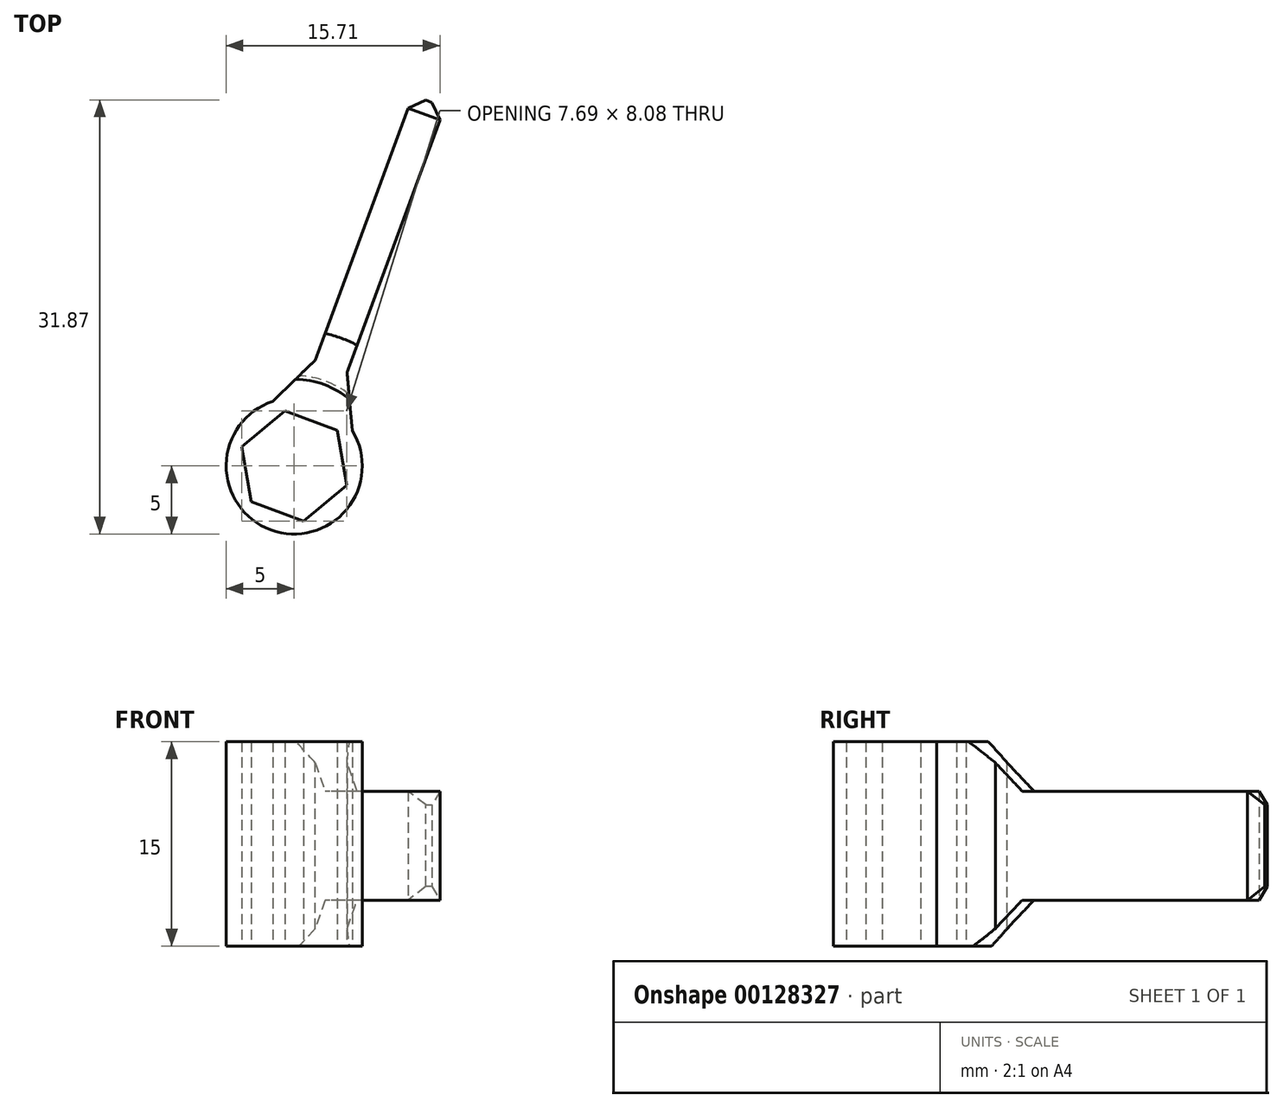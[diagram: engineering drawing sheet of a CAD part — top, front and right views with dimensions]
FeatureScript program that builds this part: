
annotation { "Feature Type Name" : "Feature", "Feature Type Description" : "" }
export const myFeature = defineFeature(function(context is Context, id is Id, definition is map)
    precondition{}
    {
        {
            var Q0;
            Q0=qCreatedBy(makeId("Top.planeOp"),FACE);
            var sketch = newSketch(context, id + "F0", { "sketchPlane" : qUnion([Q0])});
            skCircle(sketch, "E0", {"center": v(0, 0) * mm, "radius": 5 * mm});
            skCircle(sketch, "E1.cCircle", {"center": v(0, 0) * mm, "radius": 4.1 * mm, "construction": true});
            skLineSegment(sketch, "E1.0", {"start": v(3.85, -1.42) * mm, "end": v(0.7, -4.04) * mm});
            skLineSegment(sketch, "E1.1", {"start": v(0.7, -4.04) * mm, "end": v(-3.15, -2.62) * mm});
            skLineSegment(sketch, "E1.2", {"start": v(-3.15, -2.62) * mm, "end": v(-3.85, 1.42) * mm});
            skLineSegment(sketch, "E1.3", {"start": v(-3.85, 1.42) * mm, "end": v(-0.7, 4.04) * mm});
            skLineSegment(sketch, "E1.4", {"start": v(-0.7, 4.04) * mm, "end": v(3.15, 2.62) * mm});
            skLineSegment(sketch, "E1.5", {"start": v(3.15, 2.62) * mm, "end": v(3.85, -1.42) * mm});
            skSolve(sketch);
        }
        {
            var Q0;
            Q0 = qSketchRegion(id + "F0", true);
            extrude(context, id + "F1", {"entities" : qUnion([Q0]), "depth" : 15 * mm});
        }
        {
            var Q0;
            Q0=makeQuery(id+"F1.opExtrude","SWEPT_FACE",FACE,{"disambiguationData":[OSD([sQuery(id+"F0.wireOp",EDGE,"E1.4")])]});
            var sketch = newSketch(context, id + "F2", { "sketchPlane" : qUnion([Q0])});
            skLineSegment(sketch, "E2.bottom", {"start": v(1.25, 11.37) * mm, "end": v(-1.25, 11.37) * mm});
            skLineSegment(sketch, "E2.top", {"start": v(1.25, 3.37) * mm, "end": v(-1.25, 3.37) * mm});
            skLineSegment(sketch, "E2.left", {"start": v(1.25, 11.37) * mm, "end": v(1.25, 3.37) * mm});
            skLineSegment(sketch, "E2.right", {"start": v(-1.25, 11.37) * mm, "end": v(-1.25, 3.37) * mm});
            skPoint(sketch, "E3", {"position": v(0, 11.37) * mm});
            skPoint(sketch, "E4", {"position": v(0, 15) * mm});
            skSolve(sketch);
        }
        {
            var Q0;
            Q0=makeQuery(id+"F2.imprint","IMPRINT",FACE,{"disambiguationData":[TD([[makeQuery(id+"F2.imprint","IMPRINT",EDGE,{"derivedFrom":sQuery(id+"F2.wireOp",EDGE,"E2.bottom")}),1.0]])]});
            extrude(context, id + "F3", {"entities" : qUnion([Q0]), "operationType" : NewBodyOperationType.ADD, "oppositeDirection" : true, "depth" : 25 * mm});
        }
        {
            var Q0;
            Q0=makeQuery(id+"F3.boolean.opBoolean","INTERSECT",EDGE,{"derivedFrom":[makeQuery(id+"F1.opExtrude","SWEPT_FACE",FACE,{"disambiguationData":[OSD([sQuery(id+"F0.wireOp",EDGE,"E0")])]}),makeQuery(id+"F3.opExtrude","SWEPT_FACE",FACE,{"disambiguationData":[OSD([sQuery(id+"F2.wireOp",EDGE,"E2.bottom")])]})]});
            var Q1;
            Q1=makeQuery(id+"F3.boolean.opBoolean","INTERSECT",EDGE,{"derivedFrom":[makeQuery(id+"F1.opExtrude","SWEPT_FACE",FACE,{"disambiguationData":[OSD([sQuery(id+"F0.wireOp",EDGE,"E0")])]}),makeQuery(id+"F3.opExtrude","SWEPT_FACE",FACE,{"disambiguationData":[OSD([sQuery(id+"F2.wireOp",EDGE,"E2.top")])]})]});
            var Q2;
            Q2=makeQuery(id+"F3.boolean.opBoolean","INTERSECT",EDGE,{"derivedFrom":[makeQuery(id+"F1.opExtrude","SWEPT_FACE",FACE,{"disambiguationData":[OSD([sQuery(id+"F0.wireOp",EDGE,"E0")])]}),makeQuery(id+"F3.opExtrude","SWEPT_FACE",FACE,{"disambiguationData":[OSD([sQuery(id+"F2.wireOp",EDGE,"E2.right")])]})]});
            var Q3;
            Q3=makeQuery(id+"F3.boolean.opBoolean","INTERSECT",EDGE,{"derivedFrom":[makeQuery(id+"F1.opExtrude","SWEPT_FACE",FACE,{"disambiguationData":[OSD([sQuery(id+"F0.wireOp",EDGE,"E0")])]}),makeQuery(id+"F3.opExtrude","SWEPT_FACE",FACE,{"disambiguationData":[OSD([sQuery(id+"F2.wireOp",EDGE,"E2.left")])]})]});
            chamfer(context, id + "F4", {"entities" : qUnion([Q0, Q1, Q2, Q3]), "width" : 5 * mm, "tangentPropagation" : true});
        }
        {
            var Q0;
            Q0=makeQuery(id+"F3.opExtrude","CAP_FACE",FACE,{"disambiguationData":[OSD([sQuery(id+"F2.wireOp",EDGE,"E2.bottom"),sQuery(id+"F2.wireOp",EDGE,"E2.top"),sQuery(id+"F2.wireOp",EDGE,"E2.left"),sQuery(id+"F2.wireOp",EDGE,"E2.right")])],"isStart":false});
            chamfer(context, id + "F5", {"entities" : qUnion([Q0]), "width" : 1 * mm, "tangentPropagation" : true});
        }
    });
